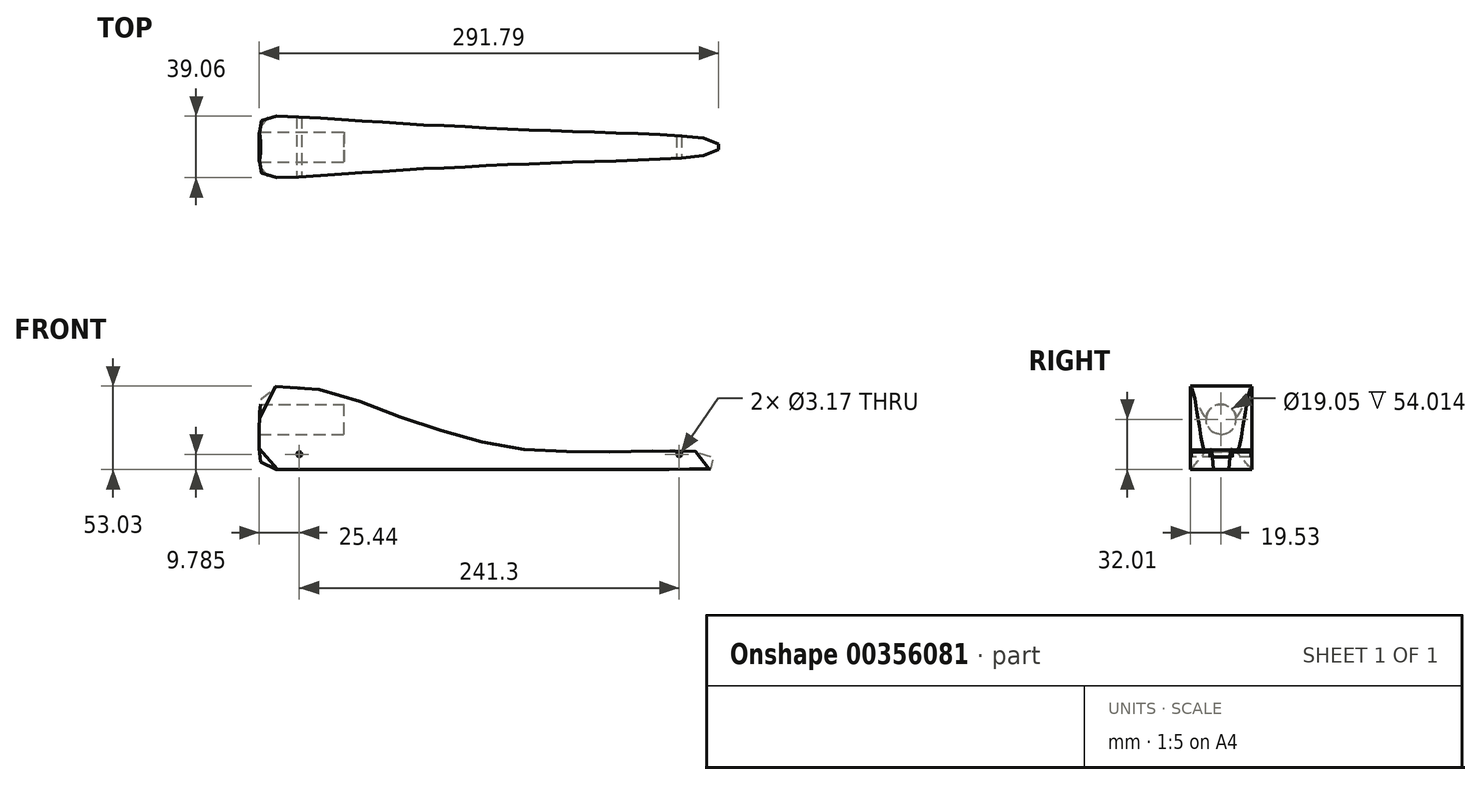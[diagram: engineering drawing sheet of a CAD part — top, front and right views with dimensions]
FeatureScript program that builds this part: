
annotation { "Feature Type Name" : "Feature", "Feature Type Description" : "" }
export const myFeature = defineFeature(function(context is Context, id is Id, definition is map)
    precondition{}
    {
        {
            var Q0;
            Q0=qCreatedBy(makeId("Front.planeOp"),FACE);
            var sketch = newSketch(context, id + "F0", { "sketchPlane" : qUnion([Q0])});
            skLineSegment(sketch, "E0.bottom", {"start": v(-146.05, 31.75) * mm, "end": v(146.05, 31.75) * mm, "construction": true});
            skLineSegment(sketch, "E0.top", {"start": v(-146.05, -31.75) * mm, "end": v(146.05, -31.75) * mm, "construction": true});
            skLineSegment(sketch, "E0.right", {"start": v(146.05, 31.75) * mm, "end": v(146.05, -31.75) * mm, "construction": true});
            skFitSpline(sketch, "E1", {"points": [v(-146.05, -19.47) * mm, v(-146.05, 0) * mm, v(-141.56, 18.66) * mm, v(-130.06, 20.95) * mm, v(-118.03, 20.43) * mm, v(-104.95, 18.33) * mm, v(-85.74, 12.66) * mm, v(-52.39, 0) * mm, v(-29.64, -7.49) * mm, v(0, -15.59) * mm, v(22.62, -19.19) * mm, v(57.5, -20.5) * mm, v(83.5, -20.63) * mm, v(104.37, -20.17) * mm, v(120.18, -19.42) * mm, v(134.46, -20.89) * mm, v(139.41, -22.4) * mm, v(144.95, -26.44) * mm, v(145.3, -30.66) * mm, v(141.58, -31.5) * mm, v(115.46, -31.76) * mm, v(90.93, -31.75) * mm, v(68.3, -31.75) * mm, v(46.54, -31.75) * mm, v(19.16, -31.75) * mm, v(-6.86, -31.75) * mm, v(-28.21, -31.75) * mm, v(-58.9, -31.75) * mm, v(-90.35, -31.75) * mm, v(-110.12, -31.75) * mm, v(-136.77, -31.87) * mm, v(-143.93, -29.62) * mm, v(-146.05, -19.47) * mm]});
            skLineSegment(sketch, "E2.bottom", {"start": v(-146.05, 9.52) * mm, "end": v(-95.25, 9.52) * mm, "construction": true});
            skLineSegment(sketch, "E2.top", {"start": v(-141.83, -9.52) * mm, "end": v(-95.25, -9.52) * mm, "construction": true});
            skLineSegment(sketch, "E2.right", {"start": v(-95.25, 9.52) * mm, "end": v(-95.25, -9.52) * mm, "construction": true});
            skLineSegment(sketch, "E3", {"start": v(-146.05, 31.75) * mm, "end": v(-146.05, -31.75) * mm, "construction": true});
            skSolve(sketch);
        }
        {
            var Q0;
            Q0=qCreatedBy(makeId("Top.planeOp"),FACE);
            var sketch = newSketch(context, id + "F1", { "sketchPlane" : qUnion([Q0])});
            skLineSegment(sketch, "E4.bottom", {"start": v(-146.05, 22.22) * mm, "end": v(146.05, 22.23) * mm, "construction": true});
            skLineSegment(sketch, "E4.top", {"start": v(-146.05, -22.23) * mm, "end": v(146.05, -22.22) * mm, "construction": true});
            skLineSegment(sketch, "E4.left", {"start": v(-146.05, 22.22) * mm, "end": v(-146.05, -22.23) * mm, "construction": true});
            skLineSegment(sketch, "E4.right", {"start": v(146.05, 22.22) * mm, "end": v(146.05, -22.22) * mm, "construction": true});
            skLineSegment(sketch, "E5", {"start": v(-146.05, 0) * mm, "end": v(146.05, 0) * mm, "construction": true});
            skFitSpline(sketch, "E6", {"points": [v(-146.05, 0) * mm, v(-144.14, 17.3) * mm, v(-134.48, 19.47) * mm, v(-110.17, 18.52) * mm, v(-88.6, 16.8) * mm, v(-64.64, 15.44) * mm, v(-42.17, 13.94) * mm, v(-24.23, 13.34) * mm, v(-5.14, 12.06) * mm, v(13.29, 11.26) * mm, v(28.57, 10.65) * mm, v(46.41, 9.93) * mm, v(69.55, 9.28) * mm, v(88.72, 8.6) * mm, v(107.2, 7.91) * mm, v(118.84, 7.23) * mm, v(127.06, 6.54) * mm, v(135.7, 5.54) * mm, v(146.05, 0) * mm], "startDerivative": vector(0.05, 335.55) * mm, "endDerivative": vector(0.95, -277.5) * mm});
            skFitSpline(sketch, "E7.MirrorCS", {"points": [v(-146.05, 0) * mm, v(-144.14, -17.3) * mm, v(-134.48, -19.47) * mm, v(-110.17, -18.52) * mm, v(-88.6, -16.8) * mm, v(-64.64, -15.44) * mm, v(-42.17, -13.94) * mm, v(-24.23, -13.34) * mm, v(-5.14, -12.06) * mm, v(13.29, -11.26) * mm, v(28.57, -10.65) * mm, v(46.41, -9.93) * mm, v(69.55, -9.28) * mm, v(88.72, -8.6) * mm, v(107.2, -7.91) * mm, v(118.84, -7.23) * mm, v(127.06, -6.54) * mm, v(135.7, -5.54) * mm, v(146.05, 0) * mm], "startDerivative": vector(0.05, -335.55) * mm, "endDerivative": vector(0.95, 277.5) * mm});
            skLineSegment(sketch, "E8.MirrorCS", {"start": v(-146.05, -22.23) * mm, "end": v(146.05, -22.23) * mm});
            skSolve(sketch);
        }
        {
            var Q0;
            Q0=qCreatedBy(makeId("Right.planeOp"),FACE);
            var sketch = newSketch(context, id + "F2", { "sketchPlane" : qUnion([Q0])});
            skCircle(sketch, "E9", {"center": v(0, 0) * mm, "radius": 9.53 * mm});
            skSolve(sketch);
        }
        {
            var Q0;
            Q0=qCreatedBy(makeId("Front.planeOp"),FACE);
            var sketch = newSketch(context, id + "F3", { "sketchPlane" : qUnion([Q0])});
            skCircle(sketch, "E10", {"center": v(-120.65, -22.22) * mm, "radius": 1.59 * mm});
            skCircle(sketch, "E11", {"center": v(120.65, -22.23) * mm, "radius": 1.59 * mm});
            skSolve(sketch);
        }
        {
            var Q0;
            Q0=qSketchRegion(id+"F0",true);
            extrude(context, id + "F4", {"entities" : qUnion([Q0]), "depth" : 44.45 * mm, "symmetric" : true});
        }
        {
            var Q0;
            Q0=qSketchRegion(id+"F1",true);
            extrude(context, id + "F5", {"entities" : qUnion([Q0]), "operationType" : NewBodyOperationType.INTERSECT, "endBound" : BoundingType.THROUGH_ALL, "oppositeDirection" : true, "depth" : 60.96 * mm, "hasSecondDirection" : true, "secondDirectionBound" : BoundingType.THROUGH_ALL, "secondDirectionOppositeDirection" : false, "secondDirectionDepth" : 25.4 * mm});
        }
        {
            var Q0;
            Q0=qSketchRegion(id+"F2",true);
            extrude(context, id + "F6", {"entities" : qUnion([Q0]), "operationType" : NewBodyOperationType.REMOVE, "oppositeDirection" : true, "depth" : 152.4 * mm, "hasSecondDirection" : true, "secondDirectionOppositeDirection" : true, "secondDirectionDepth" : 92.07 * mm});
        }
        {
            var Q0;
            Q0=qSketchRegion(id+"F3",true);
            extrude(context, id + "F7", {"entities" : qUnion([Q0]), "operationType" : NewBodyOperationType.REMOVE, "oppositeDirection" : true, "depth" : 50.8 * mm, "symmetric" : true});
        }
    });
